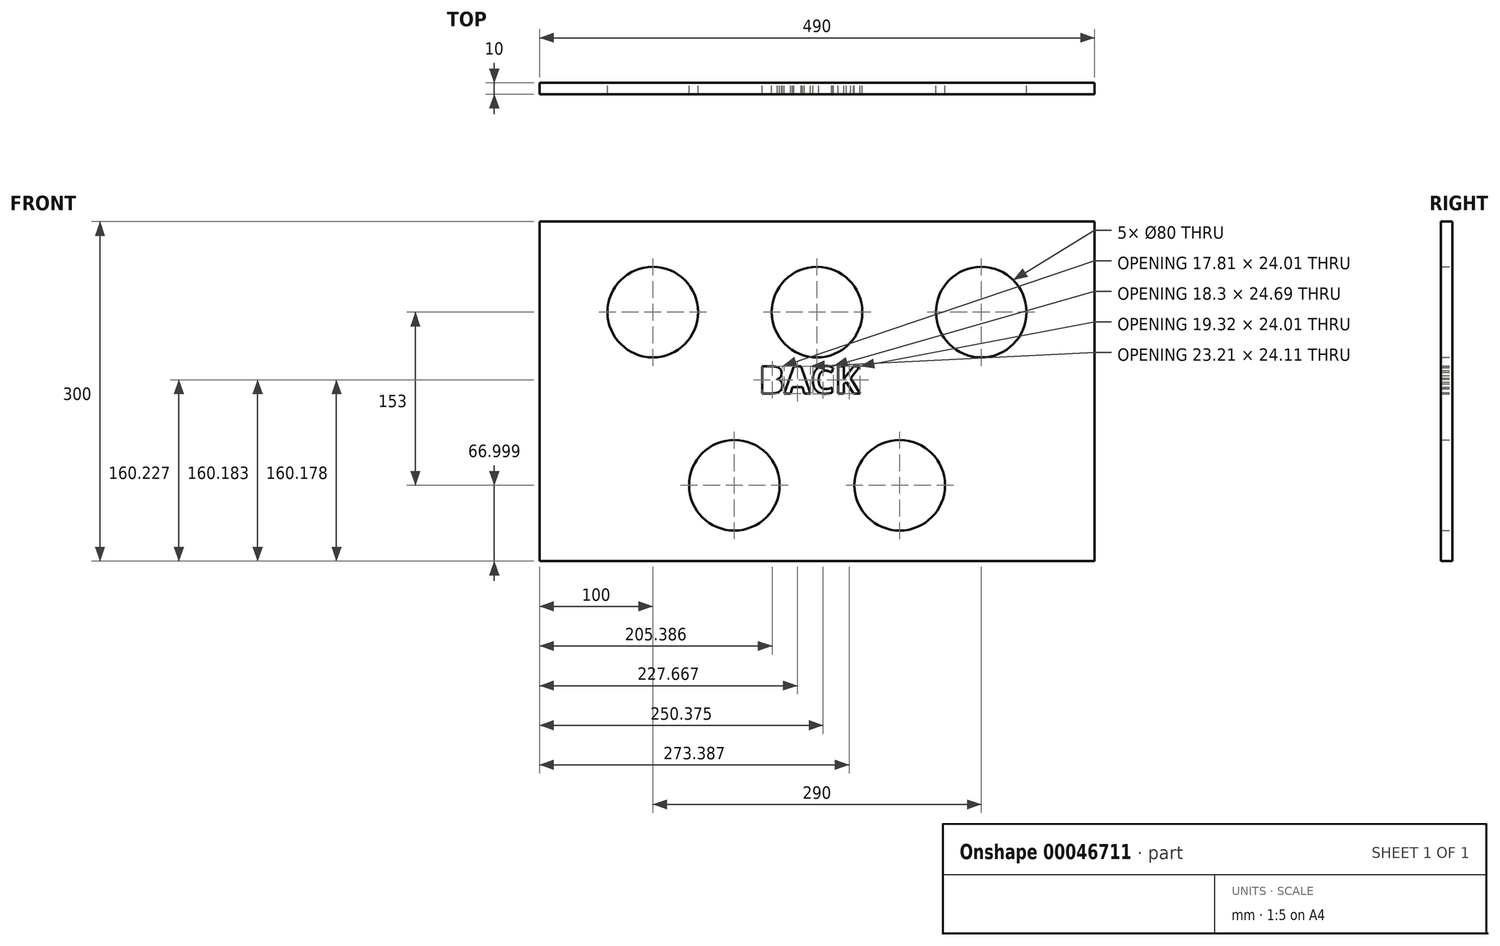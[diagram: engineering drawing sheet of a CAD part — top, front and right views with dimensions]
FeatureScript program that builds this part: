
annotation { "Feature Type Name" : "Feature", "Feature Type Description" : "" }
export const myFeature = defineFeature(function(context is Context, id is Id, definition is map)
    precondition{}
    {
        {
            var Q0;
            Q0=qCreatedBy(makeId("Front.planeOp"),FACE);
            var sketch = newSketch(context, id + "F0", { "sketchPlane" : qUnion([Q0])});
            skLineSegment(sketch, "E0.bottom", {"start": v(-245.4, 189.1) * mm, "end": v(244.6, 189.1) * mm});
            skLineSegment(sketch, "E0.top", {"start": v(-245.4, -110.9) * mm, "end": v(244.6, -110.9) * mm});
            skLineSegment(sketch, "E0.left", {"start": v(-245.4, 189.1) * mm, "end": v(-245.4, -110.9) * mm});
            skLineSegment(sketch, "E0.right", {"start": v(244.6, 189.1) * mm, "end": v(244.6, -110.9) * mm});
            skLineSegment(sketch, "E1", {"start": v(-0.4, 247.27) * mm, "end": v(-0.4, -165.89) * mm, "construction": true});
            skLineSegment(sketch, "E2", {"start": v(-305.76, 23.1) * mm, "end": v(335.35, 23.1) * mm, "construction": true});
            skCircle(sketch, "E3", {"center": v(-145.4, 109.1) * mm, "radius": 40 * mm});
            skCircle(sketch, "E4", {"center": v(-73.4, -43.9) * mm, "radius": 40 * mm});
            skCircle(sketch, "E5", {"center": v(-0.4, 109.1) * mm, "radius": 40 * mm});
            skCircle(sketch, "E6", {"center": v(72.6, -43.9) * mm, "radius": 40 * mm});
            skCircle(sketch, "E7", {"center": v(144.6, 109.1) * mm, "radius": 40 * mm});
            skText(sketch, "E8", { "text": "BACK", "fontName": "OpenSans-Bold.ttf"});
            const initialGuessF0  = {"E8": [-0.05194, 0.03727, 1, 0, 0.02422]};
            skSetInitialGuess(sketch, initialGuessF0);
            skSolve(sketch);
        }
        {
            var Q0;
            Q0=makeQuery(id+"F0.imprint","IMPRINT",FACE,{"disambiguationData":[TD([[makeQuery(id+"F0.imprint","IMPRINT",EDGE,{"derivedFrom":sQuery(id+"F0.wireOp",EDGE,"E0.bottom")}),-1.0]])]});
            extrude(context, id + "F1", {"entities" : qUnion([Q0]), "depth" : 10 * mm});
        }
    });
